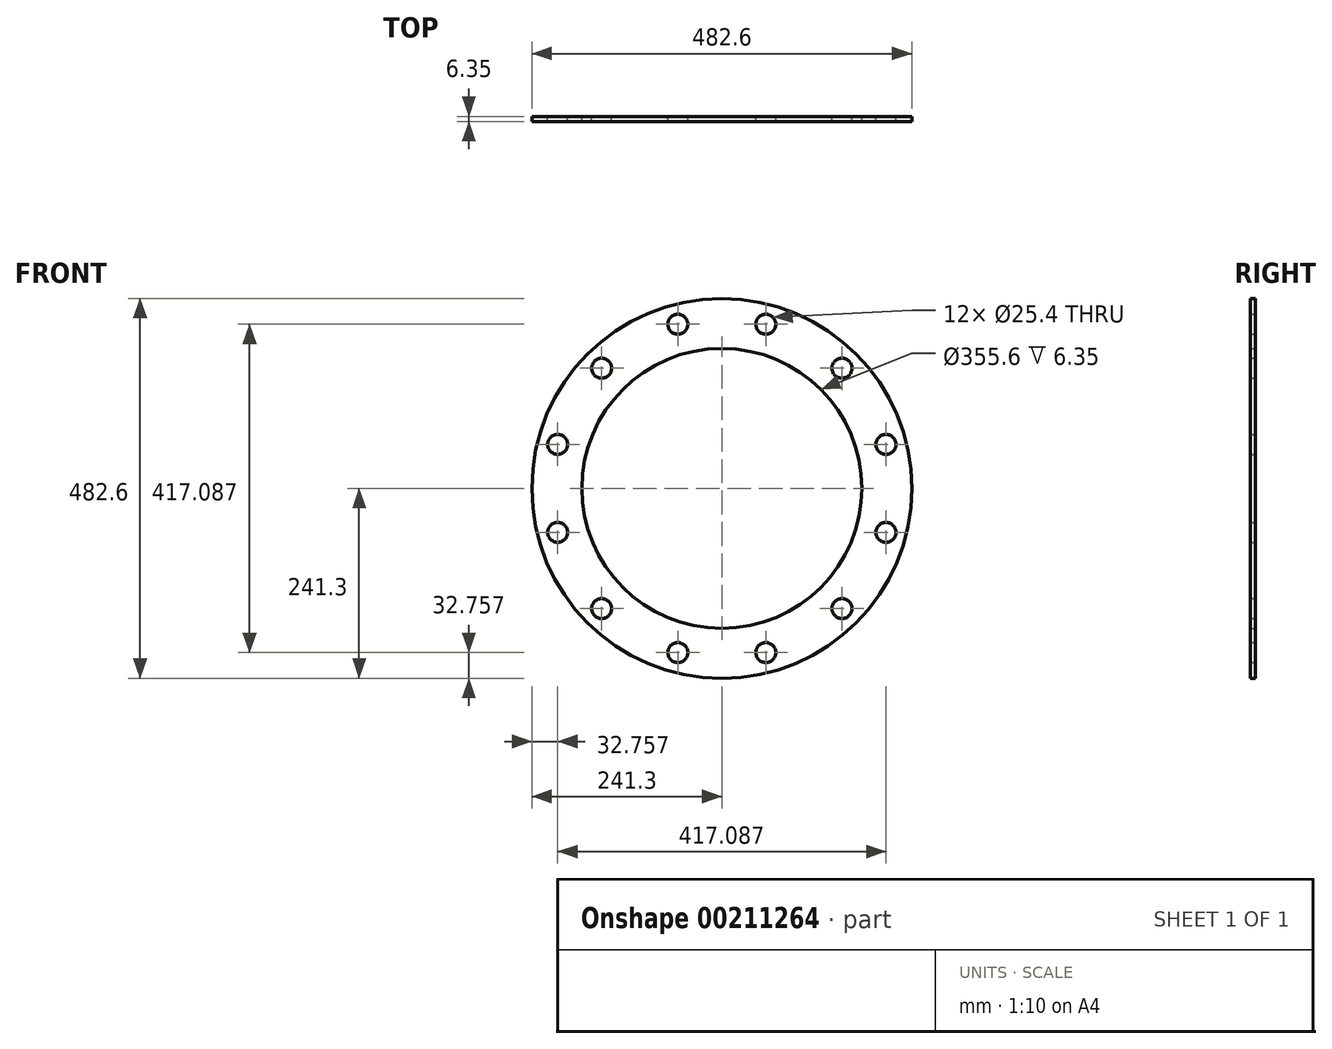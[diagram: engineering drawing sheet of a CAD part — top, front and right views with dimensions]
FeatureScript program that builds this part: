
annotation { "Feature Type Name" : "Feature", "Feature Type Description" : "" }
export const myFeature = defineFeature(function(context is Context, id is Id, definition is map)
    precondition{}
    {
        {
            var Q0;
            Q0=qCreatedBy(makeId("Front.planeOp"),FACE);
            var sketch = newSketch(context, id + "F0", { "sketchPlane" : qUnion([Q0])});
            skCircle(sketch, "E0", {"center": v(0, 0) * mm, "radius": 241.3 * mm});
            skCircle(sketch, "E1", {"center": v(0, 0) * mm, "radius": 177.8 * mm});
            skLineSegment(sketch, "E2", {"start": v(0, 0) * mm, "end": v(0, 9.22) * mm});
            skCircle(sketch, "E3", {"center": v(55.88, 208.54) * mm, "radius": 12.7 * mm});
            skCircle(sketch, "E4.1.0", {"center": v(-55.88, 208.54) * mm, "radius": 12.7 * mm});
            skCircle(sketch, "E4.2.0", {"center": v(-152.66, 152.66) * mm, "radius": 12.7 * mm});
            skCircle(sketch, "E4.3.0", {"center": v(-208.54, 55.88) * mm, "radius": 12.7 * mm});
            skCircle(sketch, "E4.4.0", {"center": v(-208.54, -55.88) * mm, "radius": 12.7 * mm});
            skCircle(sketch, "E4.5.0", {"center": v(-152.66, -152.66) * mm, "radius": 12.7 * mm});
            skCircle(sketch, "E4.6.0", {"center": v(-55.88, -208.54) * mm, "radius": 12.7 * mm});
            skCircle(sketch, "E4.7.0", {"center": v(55.88, -208.54) * mm, "radius": 12.7 * mm});
            skCircle(sketch, "E4.8.0", {"center": v(152.66, -152.66) * mm, "radius": 12.7 * mm});
            skCircle(sketch, "E4.9.0", {"center": v(208.54, -55.88) * mm, "radius": 12.7 * mm});
            skCircle(sketch, "E4.10.0", {"center": v(208.54, 55.88) * mm, "radius": 12.7 * mm});
            skCircle(sketch, "E4.11.0", {"center": v(152.66, 152.66) * mm, "radius": 12.7 * mm});
            skSolve(sketch);
        }
        {
            var Q0;
            Q0 = qSketchRegion(id + "F0", true);
            extrude(context, id + "F1", {"entities" : qUnion([Q0]), "depth" : 6.35 * mm});
        }
    });
